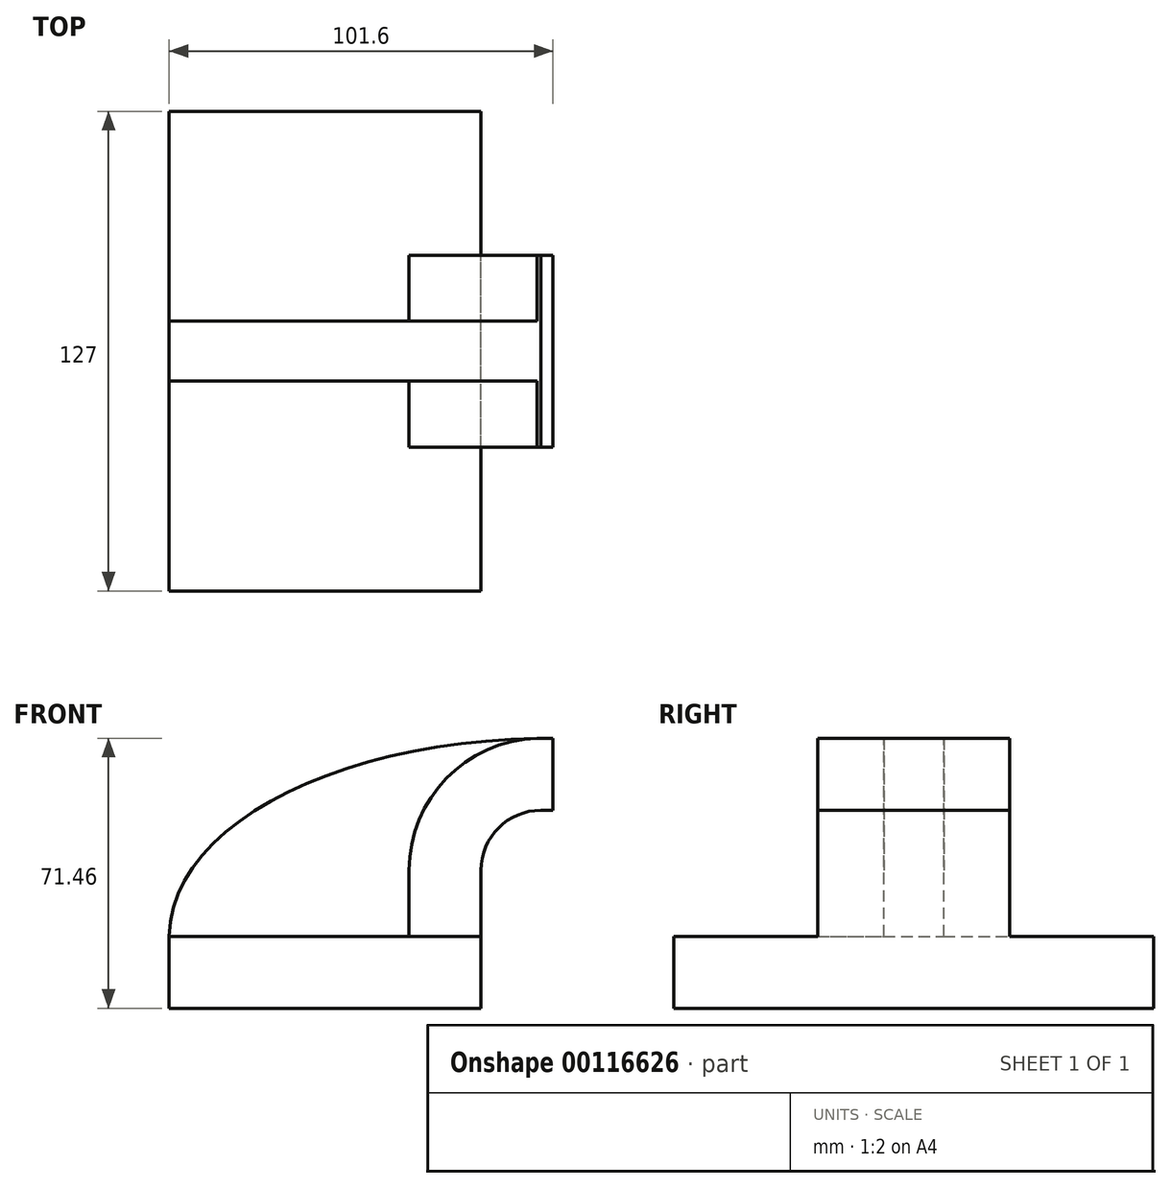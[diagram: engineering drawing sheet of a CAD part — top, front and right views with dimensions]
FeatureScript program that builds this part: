
annotation { "Feature Type Name" : "Feature", "Feature Type Description" : "" }
export const myFeature = defineFeature(function(context is Context, id is Id, definition is map)
    precondition{}
    {
        {
            var Q0;
            Q0=qCreatedBy(makeId("Front.planeOp"),FACE);
            var sketch = newSketch(context, id + "F0", { "sketchPlane" : qUnion([Q0])});
            skLineSegment(sketch, "E0.bottom", {"start": v(-41.28, 9.52) * mm, "end": v(41.27, 9.53) * mm});
            skLineSegment(sketch, "E0.top", {"start": v(-41.28, -9.53) * mm, "end": v(41.28, -9.53) * mm});
            skLineSegment(sketch, "E0.left", {"start": v(-41.28, 9.52) * mm, "end": v(-41.28, -9.53) * mm});
            skLineSegment(sketch, "E0.right", {"start": v(41.27, 9.53) * mm, "end": v(41.28, -9.52) * mm});
            skPoint(sketch, "E0.middle", {"position": v(0, 0) * mm});
            skLineSegment(sketch, "E1.bottom", {"start": v(60.32, 38.1) * mm, "end": v(111.12, 38.1) * mm});
            skLineSegment(sketch, "E1.top", {"start": v(60.32, 66.68) * mm, "end": v(111.12, 66.68) * mm});
            skLineSegment(sketch, "E1.left", {"start": v(60.32, 38.1) * mm, "end": v(60.32, 66.68) * mm});
            skLineSegment(sketch, "E1.right", {"start": v(111.12, 38.1) * mm, "end": v(111.12, 66.68) * mm});
            skPoint(sketch, "E1.middle", {"position": v(85.72, 52.39) * mm});
            skLineSegment(sketch, "E2", {"start": v(41.27, 9.53) * mm, "end": v(41.27, 27) * mm});
            skArc(sketch, "E3", {"start": v(41.28, 27) * mm, "mid": v(45.92, 38.23) * mm, "end": v(57.15, 42.88) * mm});
            skLineSegment(sketch, "E4", {"start": v(57.15, 42.88) * mm, "end": v(60.32, 42.88) * mm});
            skLineSegment(sketch, "E5", {"start": v(60.32, 42.88) * mm, "end": v(112.48, 42.88) * mm});
            skLineSegment(sketch, "E6.0", {"start": v(60.32, 61.93) * mm, "end": v(112.48, 61.93) * mm});
            skLineSegment(sketch, "E6.1", {"start": v(57.15, 61.93) * mm, "end": v(60.32, 61.93) * mm});
            skArc(sketch, "E6.2", {"start": v(22.23, 27) * mm, "mid": v(32.45, 51.7) * mm, "end": v(57.15, 61.93) * mm});
            skLineSegment(sketch, "E6.3", {"start": v(22.22, 9.53) * mm, "end": v(22.22, 27) * mm});
            skLineSegment(sketch, "E7", {"start": v(85.72, 52.39) * mm, "end": v(85.72, 61.93) * mm});
            skPoint(sketch, "E7.endSnap0", {"position": v(86.4, 61.93) * mm});
            skLineSegment(sketch, "E8", {"start": v(85.72, 61.93) * mm, "end": v(85.72, 52.39) * mm});
            skLineSegment(sketch, "E9", {"start": v(85.72, 52.39) * mm, "end": v(85.72, 42.88) * mm});
            skFitSpline(sketch, "E10", {"points": [v(-41.28, 9.52) * mm, v(57.15, 61.93) * mm], "startDerivative": vector(1.73, 89.88) * mm, "endDerivative": vector(159.4, 1.97) * mm});
            skSolve(sketch);
        }
        {
            var Q0;
            Q0=makeQuery(id+"F0.imprint","IMPRINT",FACE,{"disambiguationData":[TD([[makeQuery(id+"F0.imprint","IMPRINT",EDGE,{"derivedFrom":sQuery(id+"F0.wireOp",EDGE,"E0.top")}),1.0]])]});
            extrude(context, id + "F1", {"entities" : qUnion([Q0]), "endBound" : BoundingType.SYMMETRIC, "depth" : 127 * mm});
        }
        {
            var Q0;
            {var subQ0=sQuery(id+"F0.wireOp",EDGE,"E2");Q0=makeQuery(id+"F0.imprint","IMPRINT",FACE,{"disambiguationData":[TD([[makeQuery(id+"F0.imprint","IMPRINT",EDGE,{"derivedFrom":subQ0}),1.0]])]});}
            var Q1;
            {var subQ3=sQuery(id+"F0.wireOp",EDGE,"E8");Q1=makeQuery(id+"F0.imprint","IMPRINT",FACE,{"disambiguationData":[TD([[makeQuery(id+"F0.imprint","IMPRINT",EDGE,{"derivedFrom":subQ3}),-1.0]])]});}
            var Q2;
            {var subQ0=sQuery(id+"F0.wireOp",EDGE,"E8");Q2=makeQuery(id+"F0.imprint","IMPRINT",FACE,{"disambiguationData":[TD([[makeQuery(id+"F0.imprint","IMPRINT",EDGE,{"derivedFrom":subQ0}),1.0]])]});}
            extrude(context, id + "F2", {"entities" : qUnion([Q0, Q1, Q2]), "operationType" : NewBodyOperationType.ADD, "endBound" : BoundingType.SYMMETRIC, "depth" : 50.8 * mm});
        }
        {
            var Q0;
            {var subQ3=sQuery(id+"F0.wireOp",EDGE,"E6.3");Q0=makeQuery(id+"F0.imprint","IMPRINT",FACE,{"disambiguationData":[TD([[makeQuery(id+"F0.imprint","IMPRINT",EDGE,{"derivedFrom":subQ3}),1.0]])]});}
            extrude(context, id + "F3", {"entities" : qUnion([Q0]), "operationType" : NewBodyOperationType.ADD, "endBound" : BoundingType.SYMMETRIC, "depth" : 15.88 * mm});
        }
    });
